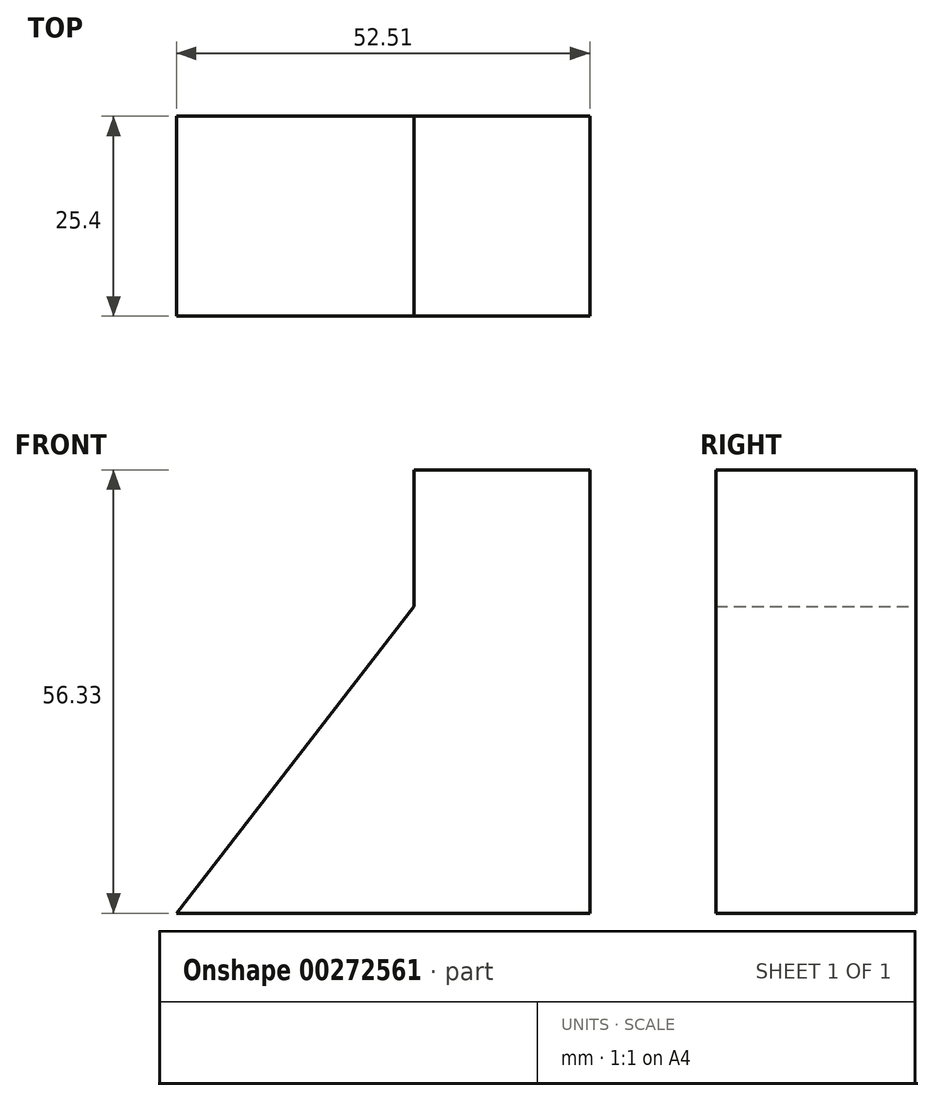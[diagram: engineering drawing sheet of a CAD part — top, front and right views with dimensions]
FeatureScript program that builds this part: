
annotation { "Feature Type Name" : "Feature", "Feature Type Description" : "" }
export const myFeature = defineFeature(function(context is Context, id is Id, definition is map)
    precondition{}
    {
        {
            var Q0;
            Q0=qCreatedBy(makeId("Front.planeOp"),FACE);
            var sketch = newSketch(context, id + "F0", { "sketchPlane" : qUnion([Q0])});
            skLineSegment(sketch, "E0", {"start": v(0, 0) * mm, "end": v(52.51, 0) * mm});
            skLineSegment(sketch, "E1", {"start": v(52.51, 0) * mm, "end": v(52.51, 56.33) * mm});
            skLineSegment(sketch, "E2", {"start": v(52.51, 56.33) * mm, "end": v(30.17, 56.33) * mm});
            skLineSegment(sketch, "E3", {"start": v(30.17, 56.33) * mm, "end": v(30.17, 38.95) * mm});
            skLineSegment(sketch, "E4", {"start": v(30.17, 38.95) * mm, "end": v(0, 0) * mm});
            skSolve(sketch);
        }
        {
            var Q0;
            Q0=makeQuery(id+"F0.imprint","IMPRINT",FACE,{"disambiguationData":[TD([[makeQuery(id+"F0.imprint","IMPRINT",EDGE,{"derivedFrom":sQuery(id+"F0.wireOp",EDGE,"E0")}),1.0]])]});
            extrude(context, id + "F1", {"entities" : qUnion([Q0]), "depth" : 25.4 * mm});
        }
    });
